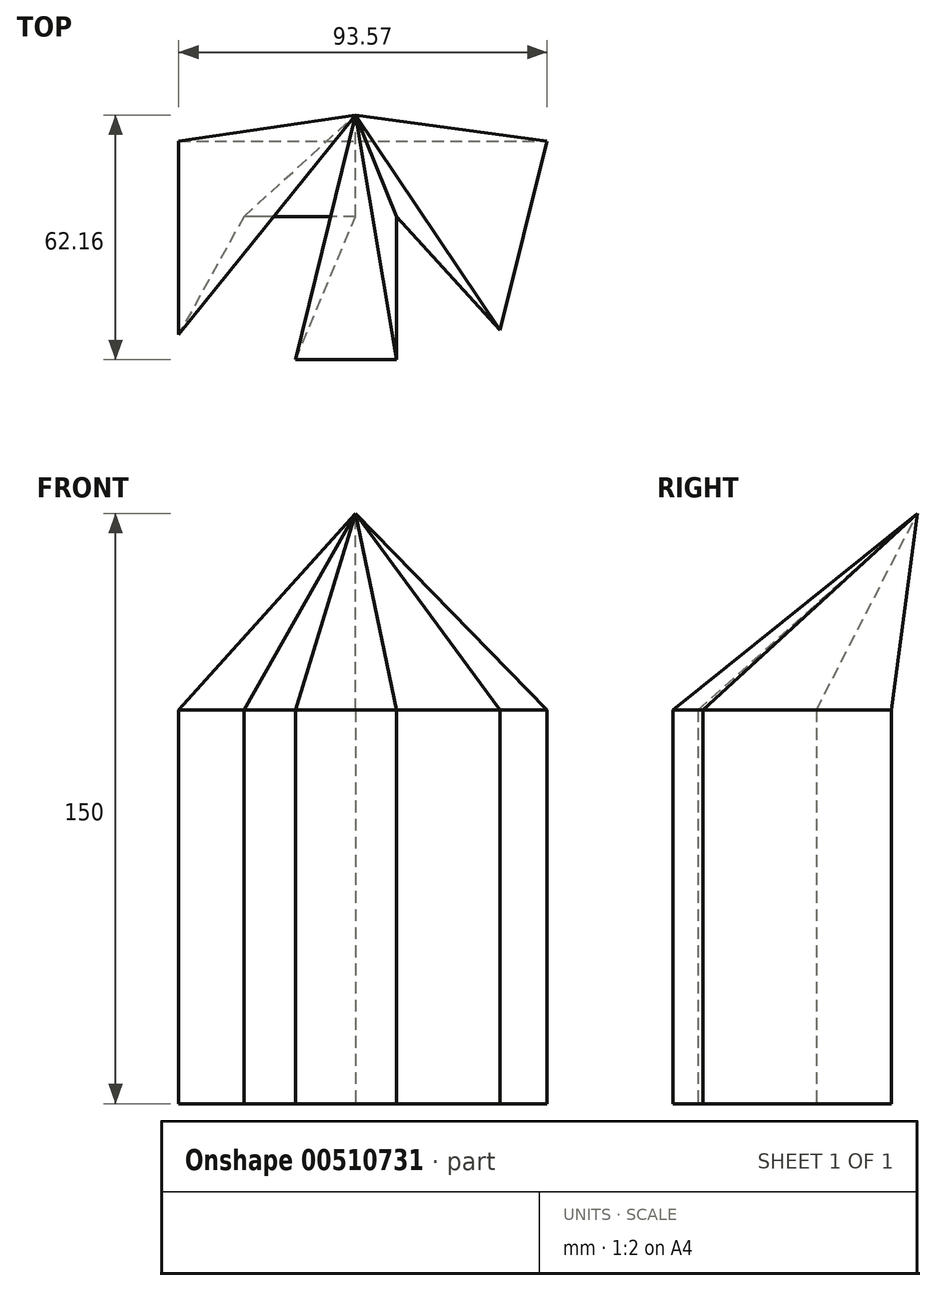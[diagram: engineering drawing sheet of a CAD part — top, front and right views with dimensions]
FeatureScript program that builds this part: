
annotation { "Feature Type Name" : "Feature", "Feature Type Description" : "" }
export const myFeature = defineFeature(function(context is Context, id is Id, definition is map)
    precondition{}
    {
        {
            var Q0;
            Q0=qCreatedBy(makeId("Top.planeOp"),FACE);
            var sketch = newSketch(context, id + "F0", { "sketchPlane" : qUnion([Q0])});
            skLineSegment(sketch, "E0", {"start": v(-45.47, 0) * mm, "end": v(48.68, 0) * mm});
            skLineSegment(sketch, "E1", {"start": v(48.68, 0) * mm, "end": v(36.73, -47.95) * mm});
            skLineSegment(sketch, "E2", {"start": v(36.73, -47.95) * mm, "end": v(10.5, -19.1) * mm});
            skLineSegment(sketch, "E3", {"start": v(10.5, -19.1) * mm, "end": v(10.5, -55.53) * mm});
            skLineSegment(sketch, "E4", {"start": v(10.5, -55.53) * mm, "end": v(-15.16, -55.53) * mm});
            skLineSegment(sketch, "E5", {"start": v(-15.16, -55.53) * mm, "end": v(0, -19.1) * mm});
            skLineSegment(sketch, "E6", {"start": v(0, -19.1) * mm, "end": v(-28.27, -19.1) * mm});
            skLineSegment(sketch, "E7", {"start": v(-28.27, -19.1) * mm, "end": v(-44.89, -49.11) * mm});
            skLineSegment(sketch, "E8", {"start": v(-44.89, -49.11) * mm, "end": v(-44.89, 0) * mm});
            skSolve(sketch);
        }
        {
            var Q0;
            {var subQ0=sQuery(id+"F0.wireOp",EDGE,"E1");Q0=makeQuery(id+"F0.imprint","IMPRINT",FACE,{"disambiguationData":[TD([[makeQuery(id+"F0.imprint","IMPRINT",EDGE,{"derivedFrom":subQ0}),-1.0]])]});}
            extrude(context, id + "F1", {"entities" : qUnion([Q0]), "endBound" : BoundingType.SYMMETRIC, "depth" : 100 * mm});
        }
        {
            var Q0;
            Q0=qCreatedBy(makeId("Top.planeOp"),FACE);
            cPlane(context, id + "F2", {"entities" : qUnion([Q0]), "cplaneType" : CPlaneType.OFFSET, "offset" : 100 * mm, "width" : 150 * mm, "height" : 150 * mm});
        }
        {
            var Q0;
            Q0=qCreatedBy(id+"F2.planeOp",FACE);
            var sketch = newSketch(context, id + "F3", { "sketchPlane" : qUnion([Q0])});
            skPoint(sketch, "E9", {"position": v(0, 6.63) * mm});
            skSolve(sketch);
        }
        {
            var Q1;
            Q1=makeQuery(id+"F1.opExtrude","CAP_FACE",FACE,{"disambiguationData":[OSD([sQuery(id+"F0.wireOp",EDGE,"E0"),sQuery(id+"F0.wireOp",EDGE,"E1"),sQuery(id+"F0.wireOp",EDGE,"E2"),sQuery(id+"F0.wireOp",EDGE,"E3"),sQuery(id+"F0.wireOp",EDGE,"E4"),sQuery(id+"F0.wireOp",EDGE,"E5"),sQuery(id+"F0.wireOp",EDGE,"E6"),sQuery(id+"F0.wireOp",EDGE,"E7"),sQuery(id+"F0.wireOp",EDGE,"E8")])],"isStart":false});
            var Q2;
            Q2=sQuery(id+"F3.wireOp",VERTEX,"E9");
            loft(context, id + "F4", {"operationType" : NewBodyOperationType.ADD, "sheetProfilesArray" : [{ "sheetProfileEntities" : qUnion([Q1]) }, { "sheetProfileEntities" : qUnion([Q2]) }]});
        }
    });
